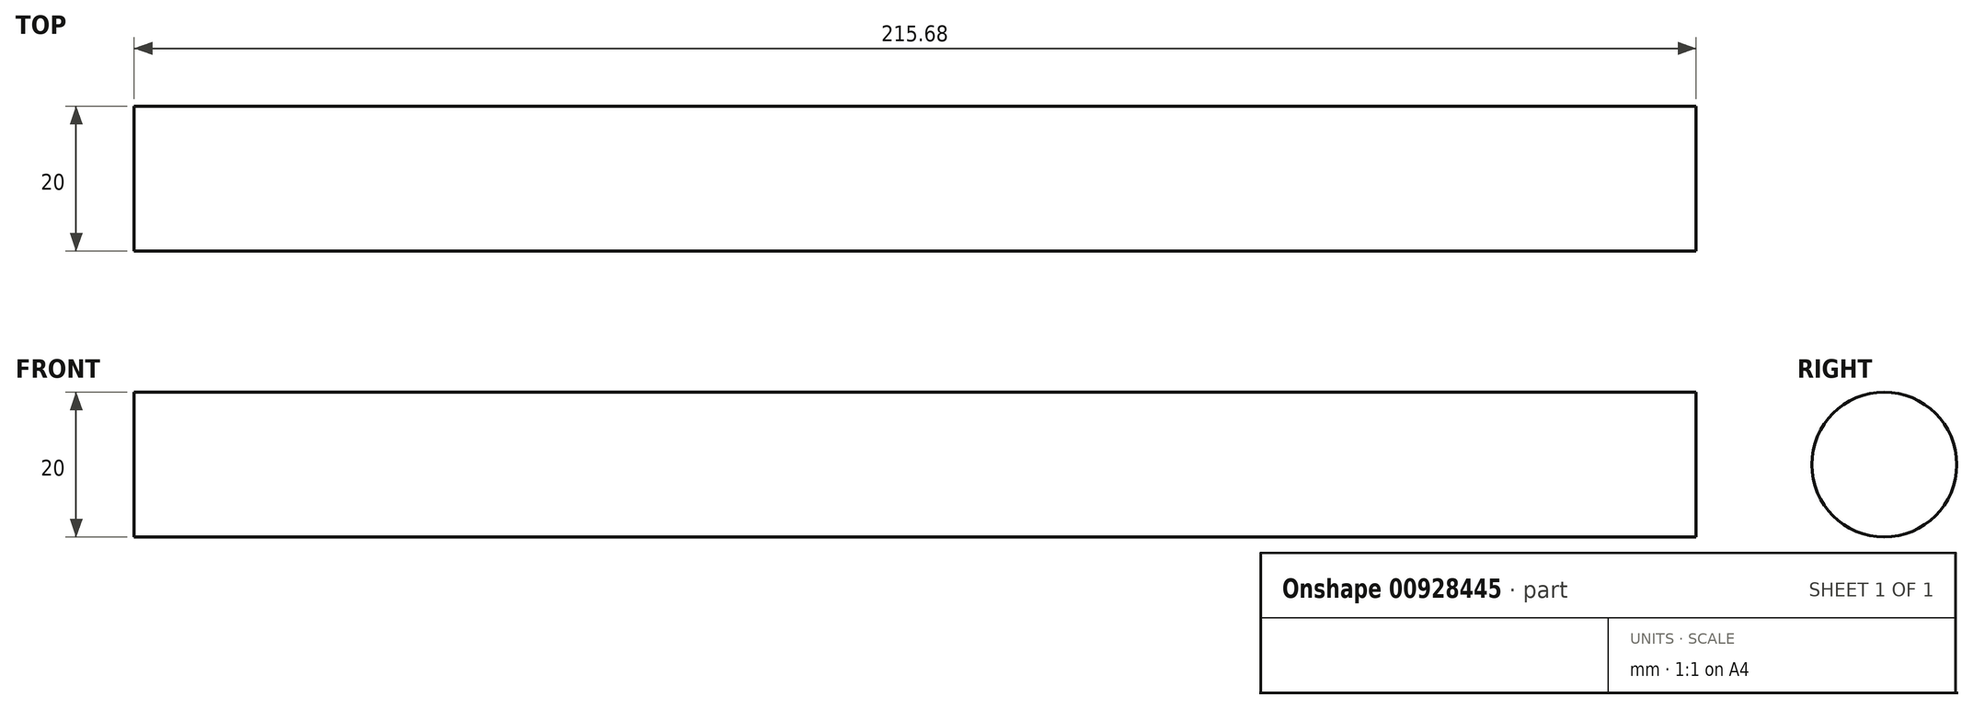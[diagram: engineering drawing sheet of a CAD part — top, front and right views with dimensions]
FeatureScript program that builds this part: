
annotation { "Feature Type Name" : "Feature", "Feature Type Description" : "" }
export const myFeature = defineFeature(function(context is Context, id is Id, definition is map)
    precondition{}
    {
        {
            var Q0;
            Q0=qCreatedBy(makeId("Right.planeOp"),FACE);
            var sketch = newSketch(context, id + "F0", { "sketchPlane" : qUnion([Q0])});
            skLineSegment(sketch, "E0", {"start": v(0, 0) * mm, "end": v(0, 273) * mm, "construction": true});
            skCircle(sketch, "E1", {"center": v(0, 273) * mm, "radius": 10 * mm});
            skSolve(sketch);
        }
        {
            var Q0;
            Q0 = qSketchRegion(id + "F0", true);
            extrude(context, id + "F1", {"entities" : qUnion([Q0]), "depth" : 107.68 * mm, "offsetDistance" : 25 * mm, "hasSecondDirection" : true, "secondDirectionOppositeDirection" : true, "secondDirectionDepth" : 108 * mm});
        }
    });
